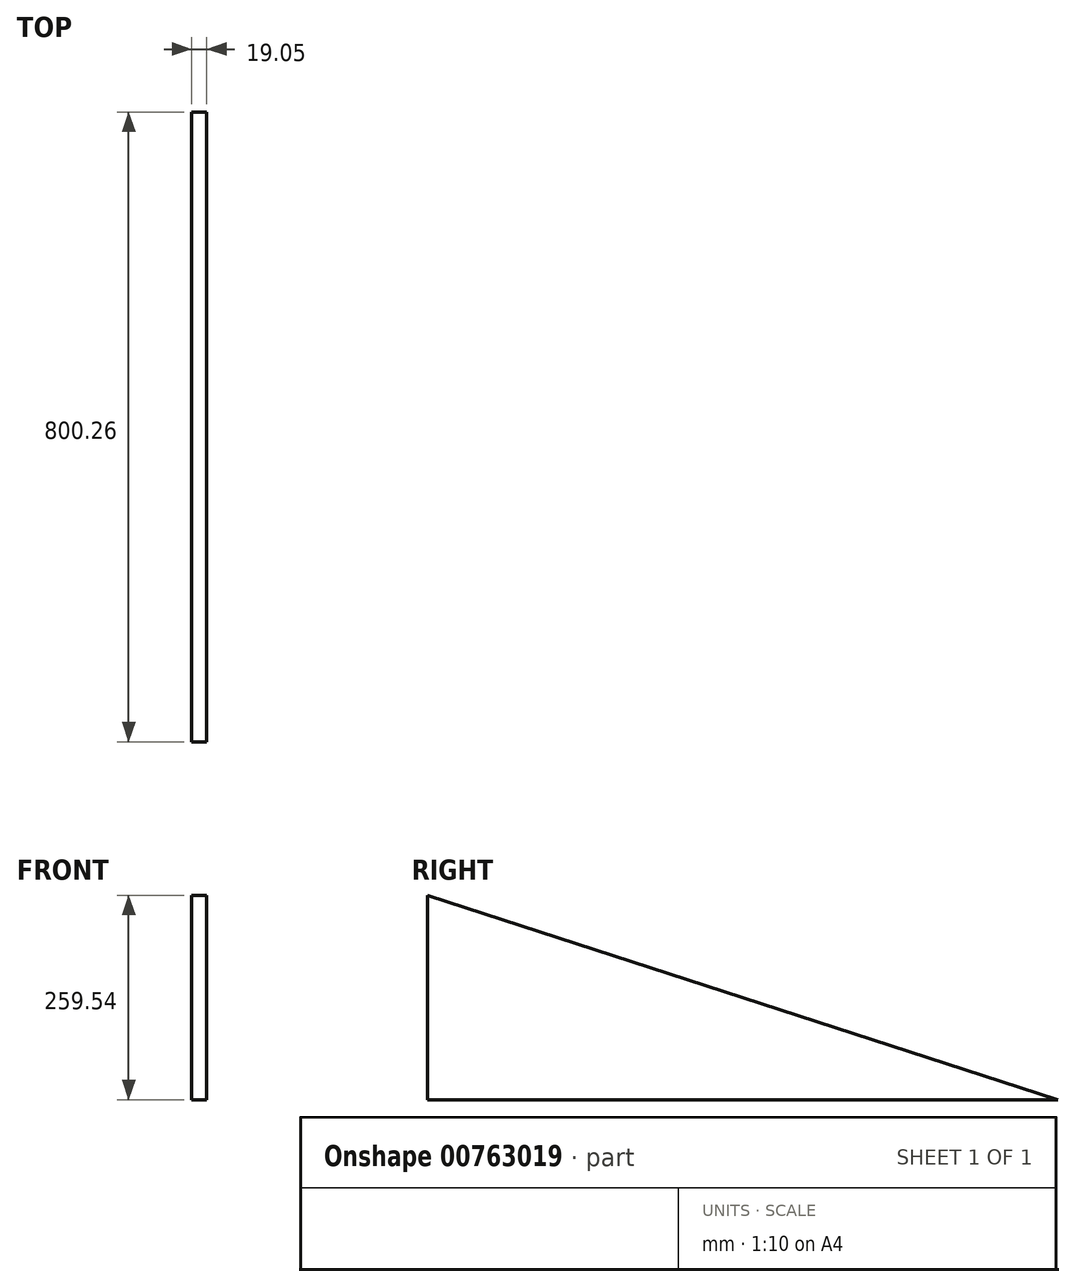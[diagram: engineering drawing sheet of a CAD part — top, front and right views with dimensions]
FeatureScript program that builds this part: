
annotation { "Feature Type Name" : "Feature", "Feature Type Description" : "" }
export const myFeature = defineFeature(function(context is Context, id is Id, definition is map)
    precondition{}
    {
        {
            var Q0;
            Q0=qCreatedBy(makeId("Right.planeOp"),FACE);
            var sketch = newSketch(context, id + "F0", { "sketchPlane" : qUnion([Q0])});
            skLineSegment(sketch, "E0.bottom", {"start": v(469.9, 152.4) * mm, "end": v(-469.9, 152.4) * mm});
            skLineSegment(sketch, "E0.top", {"start": v(469.9, -152.4) * mm, "end": v(-469.9, -152.4) * mm});
            skLineSegment(sketch, "E0.left", {"start": v(469.9, 152.4) * mm, "end": v(469.9, -152.4) * mm});
            skLineSegment(sketch, "E0.right", {"start": v(-469.9, 152.4) * mm, "end": v(-469.9, -152.4) * mm});
            skPoint(sketch, "E0.middle", {"position": v(0, 0) * mm});
            skLineSegment(sketch, "E1", {"start": v(-469.9, 152.4) * mm, "end": v(469.9, -152.4) * mm});
            skLineSegment(sketch, "E2.0", {"start": v(-450.85, 126.2) * mm, "end": v(349.41, -133.35) * mm});
            skLineSegment(sketch, "E2.1", {"start": v(-450.85, 126.2) * mm, "end": v(-450.85, -133.35) * mm});
            skLineSegment(sketch, "E2.2", {"start": v(349.41, -133.35) * mm, "end": v(-450.85, -133.35) * mm});
            skSolve(sketch);
        }
        {
            var Q0;
            Q0=makeQuery(id+"F0.imprint","IMPRINT",FACE,{"disambiguationData":[TD([[makeQuery(id+"F0.imprint","IMPRINT",EDGE,{"derivedFrom":sQuery(id+"F0.wireOp",EDGE,"E2.0")}),-1.0]])]});
            extrude(context, id + "F1", {"entities" : qUnion([Q0]), "depth" : 19.05 * mm, "offsetDistance" : 25.4 * mm});
        }
    });
